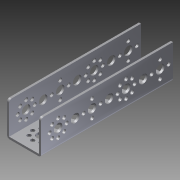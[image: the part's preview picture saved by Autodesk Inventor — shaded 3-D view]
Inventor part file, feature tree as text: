
AUTODESK INVENTOR PART (.ipt)
format: ipt  version: 2013 (Build 170138000, 138)  size: 349,184 bytes
history: native  units: in
note: dims shown in document units (in); Inventor stores cm internally (conversion verified against a paired STEP export)
features: other x1, imported_body x1, move_body x1, extrude x1, sketch x1
ambient origin geometry x8: Origin, YZ Plane, XZ Plane, XY Plane, X Axis, Y Axis, Z Axis, Center Point
feature tree (5):
  other  "CHANNEL_160_2011"
  imported_body  "Base1"
  move_body  "Move Body1"
  extrude  "Extrusion1"  Depth=0.3937in TaperAngle=0.0deg
  sketch  "Sketch3"  dims[d0=0.0in d1=0.0in d2=2.5197in d3=0.3937in d4=0.0in]
